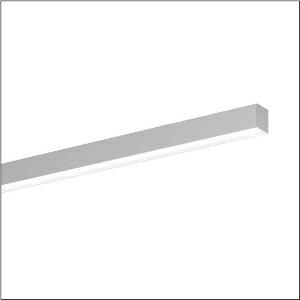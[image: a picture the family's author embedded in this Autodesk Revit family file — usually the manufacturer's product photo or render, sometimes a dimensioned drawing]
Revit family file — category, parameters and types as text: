
# Revit family: silica_r__21_51mx23db35sb_5652
name_source: partatom
category: Lighting Fixtures
units: mm (PartAtom-declared; Revit-internal decimal feet)

## family parameters
Cut with Voids When Loaded = No
Host = Face
Light Source = No
Part Type = Normal
Room Calculation Point = No
Round Connector Dimension = Use Diameter
Shared = No

## types (1)
- --- (1 x LED, 4100 lm, 30.1 W, 3000K)
    Apparent Load = 30 VA
    CIE Flux Codes = 78 96 99 100 100
    Color Rendering = 80
    Color Temperature = 3000K
    Default Elevation = 1800 mm
    Description = Silica® 21, office luminaire, primary optical cover: prismatic diffuser, of PMMA, CAT 2 (L<= 3000cd/m²), light emission: direct distribution, primary light characteristic: symmetric, installation type: surface-mounted, LED, rated luminous flux: 4.100lm, luminous efficacy: 136lm/W, light colour: 830, colour temperature: 3000K, with terminal, 3+2-pole, max. 2.5mm², mains connection: 220..240V, AC, 50/60Hz, rated input power: 30.1W, luminaire housing, of aluminium, metallic grey (RAL 9006), length: 1.504mm, width: 53mm, height: 53mm, protection rating (complete): IP20, insulation class (complete): insulation class I (protective earthing), certification: CE, permissible operating ambient temperature: 0..+35°C, standard: EN 50419, packaging unit: 1 piece
    Height = 0 mm  [stored 0 ft]
    Lamp = 1 x LED
    Lamp Light Flux = 4100 lm
    Lamp Power = 30.1 W
    Lamp count = 1
    Length = 1504 mm
    Luminous efficacy = 136 lm/W
    Manufacturer = Siteco
    ModVariant = No
    Model = 51MX23DB35SB
    Mounting Place = Ceiling
    Mounting Type = Recessed
    Number of Poles = 1
    OnlyDefault = Yes
    Power Factor = 1
    Product Name = Silica® 21
    Product group = office luminaire | ceiling recessed
    ProductGroupID = 400
    Protection Class = Protection class I
    Protection Degree = IP 20
    RLX_Detail_Level = 1
    RLX_Emergency_Light_Flux = 0 lm
    RLX_Emergency_Type = 0
    RLX_Emergency_Type_DB = No
    RlxData = <blob elided: 21285 chars, md5=3e354550>
    Socket = socket
    Standby Power = 0 W
    System Light Flux = 4100 lm
    System Power = 30 W
    Type Comments = factory setting: luminous flux: 100 % | dim-lin: 254 | 345 mA
    Type Image = l_1335933.jpg
    URL = http://relux.com
    VarID = @adj_088463
    Voltage = 0 V
    Weight = 0.00 kg
    Width = 53 mm

note: [stored X ft] marks values corroborated as IEEE doubles in the binary element streams (Revit-internal decimal feet)

## geometry (parser evidence)
native form markers: Blend x4, Sweep x10
no freeform markers — native parametric forms only
